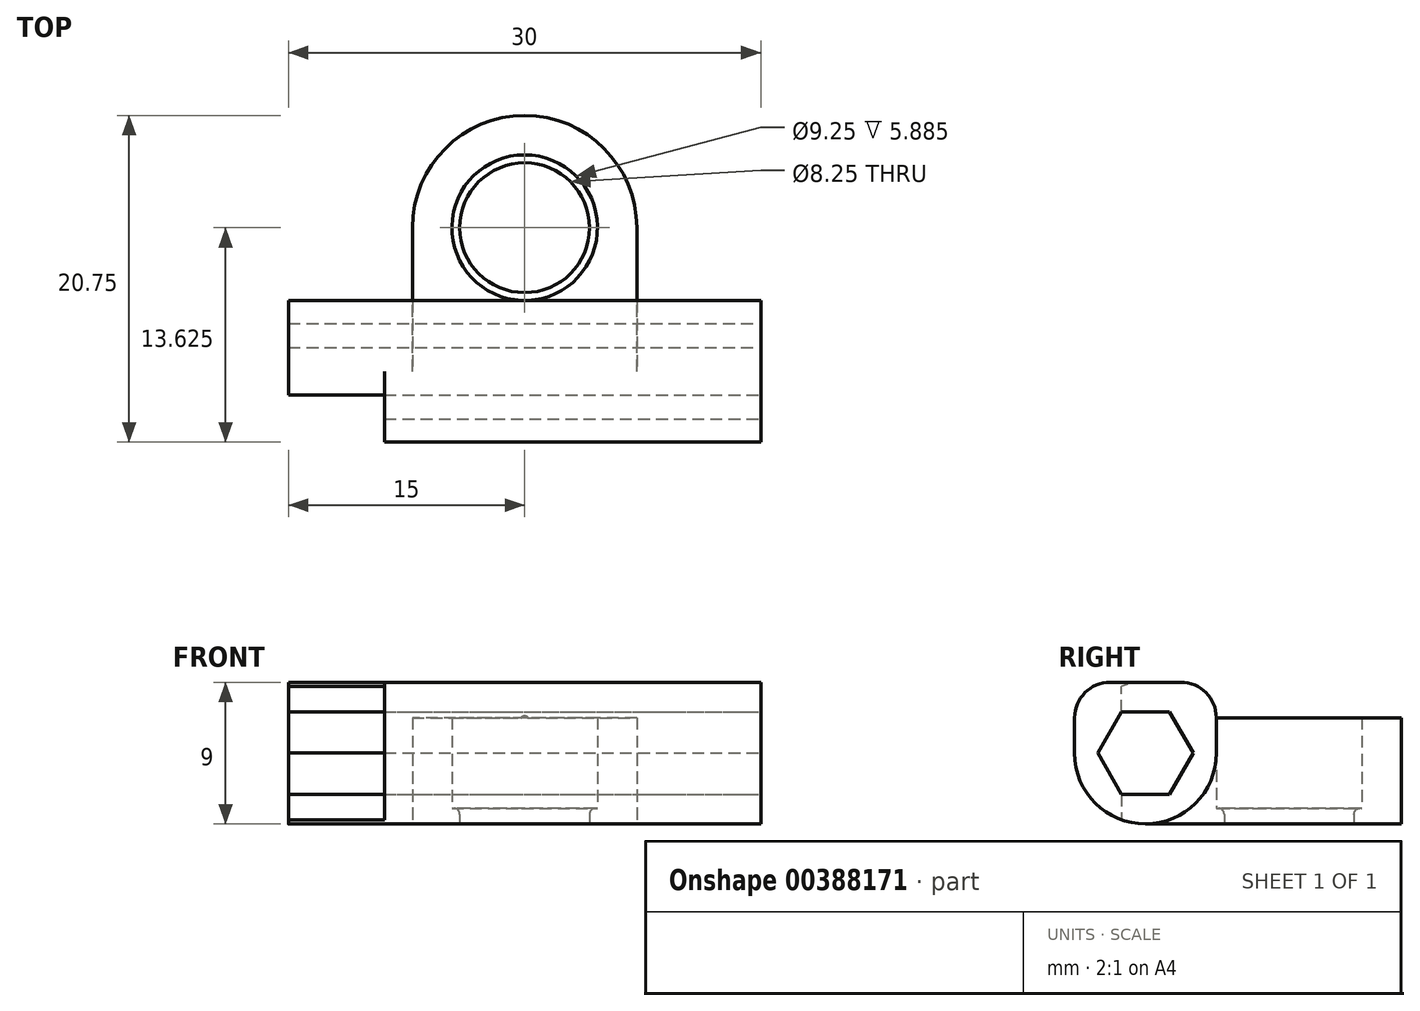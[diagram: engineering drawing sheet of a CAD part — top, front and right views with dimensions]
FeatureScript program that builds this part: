
annotation { "Feature Type Name" : "Feature", "Feature Type Description" : "" }
export const myFeature = defineFeature(function(context is Context, id is Id, definition is map)
    precondition{}
    {
        {
            var Q0;
            Q0=qCreatedBy(makeId("Top.planeOp"),FACE);
            var sketch = newSketch(context, id + "F0", { "sketchPlane" : qUnion([Q0])});
            skLineSegment(sketch, "E0", {"start": v(0, 0) * mm, "end": v(30, 0) * mm});
            skLineSegment(sketch, "E1", {"start": v(30, 0) * mm, "end": v(30, 9) * mm});
            skLineSegment(sketch, "E2", {"start": v(0, 9) * mm, "end": v(0, 0) * mm});
            skLineSegment(sketch, "E3", {"start": v(7.87, 9) * mm, "end": v(7.87, 13.62) * mm});
            skLineSegment(sketch, "E4", {"start": v(22.12, 9) * mm, "end": v(22.12, 13.62) * mm});
            skArc(sketch, "E5", {"start": v(22.12, 13.62) * mm, "mid": v(15, 20.75) * mm, "end": v(7.87, 13.62) * mm});
            skCircle(sketch, "E6", {"center": v(15, 13.62) * mm, "radius": 4.62 * mm});
            skLineSegment(sketch, "E7", {"start": v(0, 9) * mm, "end": v(7.87, 9) * mm});
            skLineSegment(sketch, "E8", {"start": v(22.12, 9) * mm, "end": v(30, 9) * mm});
            skCircle(sketch, "E9", {"center": v(15, 13.62) * mm, "radius": 4.12 * mm});
            skSolve(sketch);
        }
        {
            var Q0;
            Q0=makeQuery(id+"F0.imprint","IMPRINT",FACE,{"disambiguationData":[TD([[makeQuery(id+"F0.imprint","IMPRINT",EDGE,{"derivedFrom":sQuery(id+"F0.wireOp",EDGE,"E0")}),1.0]])]});
            extrude(context, id + "F1", {"entities" : qUnion([Q0]), "depth" : 9 * mm});
        }
        {
            var Q0;
            Q0=makeQuery(id+"F1.opExtrude","SWEPT_FACE",FACE,{"disambiguationData":[OSD([sQuery(id+"F0.wireOp",EDGE,"E1")])]});
            var sketch = newSketch(context, id + "F2", { "sketchPlane" : qUnion([Q0])});
            skCircle(sketch, "E10", {"center": v(4.5, 4.5) * mm, "radius": 4.5 * mm});
            skPoint(sketch, "E10.centerSnap0", {"position": v(0, 4.5) * mm});
            skPoint(sketch, "E10.centerSnap1", {"position": v(4.5, 9) * mm});
            skLineSegment(sketch, "E11", {"start": v(4.5, 4.5) * mm, "end": v(4.5, 7.13) * mm});
            skCircle(sketch, "E12.cCircle", {"center": v(4.5, 4.5) * mm, "radius": 2.63 * mm, "construction": true});
            skLineSegment(sketch, "E12.0", {"start": v(2.98, 7.13) * mm, "end": v(6.02, 7.13) * mm});
            skLineSegment(sketch, "E12.1", {"start": v(6.02, 7.13) * mm, "end": v(7.53, 4.5) * mm});
            skLineSegment(sketch, "E12.2", {"start": v(7.53, 4.5) * mm, "end": v(6.02, 1.88) * mm});
            skLineSegment(sketch, "E12.3", {"start": v(6.02, 1.88) * mm, "end": v(2.98, 1.87) * mm});
            skLineSegment(sketch, "E12.4", {"start": v(2.98, 1.87) * mm, "end": v(1.47, 4.5) * mm});
            skLineSegment(sketch, "E12.5", {"start": v(1.47, 4.5) * mm, "end": v(2.98, 7.13) * mm});
            skPoint(sketch, "E12.0.midPoint", {"position": v(4.5, 7.13) * mm});
            skSolve(sketch);
        }
        {
            var Q0;
            {var subQ0=sQuery(id+"F2.wireOp",EDGE,"E10");var subQ1=sQuery(id+"F0.wireOp",EDGE,"E1");var subQ4=makeQuery(id+"F1.opExtrude","CAP_EDGE",EDGE,{"disambiguationData":[OSD([subQ1])],"isStart":true});var subQ5=makeQuery(id+"F2.imprint","INTERSECT",VERTEX,{"derivedFrom":[subQ4,subQ0]});Q0=makeQuery(id+"F2.imprint","IMPRINT",FACE,{"disambiguationData":[TD([[makeQuery(id+"F2.imprint","IMPRINT",EDGE,{"disambiguationData":[TD([[subQ5,1.0]])],"derivedFrom":subQ0}),-1.0]])]});}
            var Q1;
            {var subQ0=sQuery(id+"F2.wireOp",EDGE,"E12.1");Q1=makeQuery(id+"F2.imprint","IMPRINT",FACE,{"disambiguationData":[TD([[makeQuery(id+"F2.imprint","IMPRINT",EDGE,{"derivedFrom":subQ0}),-1.0]])]});}
            extrude(context, id + "F3", {"entities" : qUnion([Q0, Q1]), "operationType" : NewBodyOperationType.REMOVE, "oppositeDirection" : true, "depth" : 30 * mm});
        }
        {
            var Q0;
            Q0=makeQuery(id+"F1.opExtrude","SWEPT_FACE",FACE,{"disambiguationData":[OSD([sQuery(id+"F0.wireOp",EDGE,"E2")])]});
            var sketch = newSketch(context, id + "F4", { "sketchPlane" : qUnion([Q0])});
            skCircle(sketch, "E13", {"center": v(-4.5, 4.5) * mm, "radius": 4.5 * mm});
            skLineSegment(sketch, "E14", {"start": v(-2.98, 1.87) * mm, "end": v(-2.98, 0.26) * mm});
            skLineSegment(sketch, "E15", {"start": v(-2.98, 7.13) * mm, "end": v(-2.98, 8.74) * mm});
            skSolve(sketch);
        }
        {
            var Q0;
            Q0=makeQuery(id+"F0.imprint","IMPRINT",FACE,{"disambiguationData":[TD([[makeQuery(id+"F0.imprint","IMPRINT",EDGE,{"derivedFrom":sQuery(id+"F0.wireOp",EDGE,"E6")}),1.0]])]});
            extrude(context, id + "F5", {"entities" : qUnion([Q0]), "operationType" : NewBodyOperationType.ADD, "depth" : 1 * mm});
        }
        {
            var Q0;
            Q0=makeQuery(id+"F1.opExtrude","CAP_FACE",FACE,{"disambiguationData":[OSD([sQuery(id+"F0.wireOp",EDGE,"E0"),sQuery(id+"F0.wireOp",EDGE,"E1"),sQuery(id+"F0.wireOp",EDGE,"E2"),sQuery(id+"F0.wireOp",EDGE,"E3"),sQuery(id+"F0.wireOp",EDGE,"E4"),sQuery(id+"F0.wireOp",EDGE,"E5"),sQuery(id+"F0.wireOp",EDGE,"E6"),sQuery(id+"F0.wireOp",EDGE,"E7"),sQuery(id+"F0.wireOp",EDGE,"E8")])],"isStart":false});
            var sketch = newSketch(context, id + "F6", { "sketchPlane" : qUnion([Q0])});
            skLineSegment(sketch, "E16", {"start": v(7.87, 9) * mm, "end": v(15.2, 9) * mm});
            skLineSegment(sketch, "E17", {"start": v(15.2, 9) * mm, "end": v(22.12, 9) * mm});
            skSolve(sketch);
        }
        {
            var Q0;
            {var subQ1=sQuery(id+"F6.wireOp",EDGE,"E17");Q0=makeQuery(id+"F6.imprint","IMPRINT",FACE,{"disambiguationData":[TD([[makeQuery(id+"F6.imprint","IMPRINT",EDGE,{"derivedFrom":subQ1}),1.0]])]});}
            extrude(context, id + "F7", {"entities" : qUnion([Q0]), "operationType" : NewBodyOperationType.REMOVE, "oppositeDirection" : true, "depth" : 2.25 * mm});
        }
        {
            var Q0;
            Q0=makeQuery(id+"F1.opExtrude","CAP_EDGE",EDGE,{"disambiguationData":[OSD([sQuery(id+"F0.wireOp",EDGE,"E8")])],"isStart":false});
            var Q1;
            Q1=makeQuery(id+"F1.opExtrude","CAP_EDGE",EDGE,{"disambiguationData":[OSD([sQuery(id+"F0.wireOp",EDGE,"E7")])],"isStart":false});
            fillet(context, id + "F8", {"entities" : qUnion([Q0, Q1]), "radius" : 2.25 * mm, "tangentPropagation" : true, "allowEdgeOverflow" : false});
        }
        {
            var Q0;
            Q0=makeQuery(id+"F1.opExtrude","CAP_EDGE",EDGE,{"disambiguationData":[OSD([sQuery(id+"F0.wireOp",EDGE,"E8")])],"isStart":true});
            var Q1;
            Q1=makeQuery(id+"F1.opExtrude","CAP_EDGE",EDGE,{"disambiguationData":[OSD([sQuery(id+"F0.wireOp",EDGE,"E7")])],"isStart":true});
            fillet(context, id + "F9", {"entities" : qUnion([Q0, Q1]), "radius" : 4.5 * mm, "tangentPropagation" : true, "allowEdgeOverflow" : false});
        }
        {
            var Q0;
            Q0=makeQuery(id+"F1.opExtrude","CAP_EDGE",EDGE,{"disambiguationData":[OSD([sQuery(id+"F0.wireOp",EDGE,"E0")])],"isStart":false});
            fillet(context, id + "F10", {"entities" : qUnion([Q0]), "radius" : 2.25 * mm, "tangentPropagation" : true, "allowEdgeOverflow" : false});
        }
        {
            var Q0;
            Q0=makeQuery(id+"F5.opExtrude","CAP_EDGE",EDGE,{"disambiguationData":[OSD([sQuery(id+"F0.wireOp",EDGE,"E9")])],"isStart":false});
            fillet(context, id + "F11", {"entities" : qUnion([Q0]), "radius" : .375 * mm, "tangentPropagation" : true, "allowEdgeOverflow" : false});
        }
        {
            var Q0;
            {var subQ1=sQuery(id+"F4.wireOp",EDGE,"E14");Q0=makeQuery(id+"F4.imprint","IMPRINT",FACE,{"disambiguationData":[TD([[makeQuery(id+"F4.imprint","IMPRINT",EDGE,{"derivedFrom":subQ1}),1.0]])]});}
            var Q1;
            {var subQ1=sQuery(id+"F0.wireOp",EDGE,"E2");var subQ2=makeQuery(id+"F1.opExtrude","SWEPT_EDGE",EDGE,{"disambiguationData":[OSD([sQuery(id+"F0.wireOp",EDGE,"E0"),subQ1])]});Q1=makeQuery(id+"F4.imprint","IMPRINT",FACE,{"disambiguationData":[TD([[makeQuery(id+"F4.imprint","IMPRINT",EDGE,{"derivedFrom":subQ2}),-1.0]])]});}
            extrude(context, id + "F12", {"entities" : qUnion([Q0, Q1]), "operationType" : NewBodyOperationType.REMOVE, "oppositeDirection" : true, "depth" : 6.1 * mm});
        }
    });
